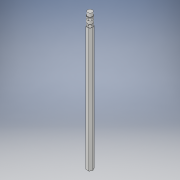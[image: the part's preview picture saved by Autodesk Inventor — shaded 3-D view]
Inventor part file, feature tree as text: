
AUTODESK INVENTOR PART (.ipt)
format: ipt  version: 2017 (Build 210142000, 142)  size: 172,032 bytes
history: native  units: in
note: dims shown in document units (in); Inventor stores cm internally (conversion verified against a paired STEP export)
features: sketch x3, other x2, extrude x1
ambient origin geometry x8: Origin, YZ Plane, XZ Plane, XY Plane, X Axis, Y Axis, Z Axis, Center Point
bodies: Solid1 (feature_tree)
feature tree (6):
  extrude  "wooden part of pencil"  Depth=0.5578in TaperAngle=0.0deg
  other  "connection for pencil and eraser"
  other  "eraser"
  sketch  "Sketch1"  dims[d0=0.023in d1=0.5578in d2=0.0in]
  sketch  "Sketch3"  dims[d3=0.0122in]
  sketch  "Sketch4"  dims[d4=0.0047in d10=0.0019in d13=0.0027in d14=0.0167in d15=0.0045in d16=0.0019in d17=0.0028in d18=0.0014in d20=0.0013in d21=0.0005in d22=0.0027in d23=0.0027in d24=0.0027in d25=0.0027in d26=0.0027in d27=0.0019in d28=0.0018in d29=0.0019in d30=90.0deg d31=0.011in d32=0.0154in d33=90.0deg]
